# Revit family: QF_COMENDA_6G3232_6G3213_
name_source: partatom
category: Attrezzature speciali
units: mm (PartAtom-declared; Revit-internal decimal feet)

## family parameters
Basato su piano di lavoro = No
Condiviso = No
Numero OmniClass = 23.40.40.14
Punto di calcolo locali = No
Quota connettore circolare = Usa diametro
Sempre verticale = Sì
Taglio con vuoti quando caricato = No
Tipo di parte = Normale
Titolo OmniClass = Food Service Equipment

## types (2) — shared parameters
Altezza allacciamento elettrico da pavimento finito = 365 mm  [stored 1.19751 ft]
Altezza da terra raccordo acqua calda = 230 mm  [stored 0.754593 ft]
Altezza dello scarico diretto acqua da pavimento finito = 230 mm  [stored 0.754593 ft]
Corrente di funzionamento normale = 12 A
Diametro dello scarico diretto di acqua = 1 1/2"
Diametro raccordo acqua calda = 1"
Fase = 3
Frequenza = 50 Hz
Lunghezza = 740 mm  [stored 2.42782 ft]
Numero dei poli = 3
Peso netto = 150.00 kg
Potenza elettrica = 7500 W
Pressione minima acqua calda = 2000.0 Pa
Produttore = COMENDA
Profondità = 845 mm  [stored 2.77231 ft]
Protezione contro le sovracorrenti = 16 A
Temperatura raccomandata per acqua calda = 50 °C
URL = www.comenda.eu
URL catalogo = https://comenda.eu
zero-valued in all types: Prospetto di default

## per-type parameters (varying)
| type | Altezza | Descrizione | Modello | Tensione |
| 6G3232 | 1695 mm | THREE-PHASE FRONT LOADING POTWASHER  WITH RCD | G-EVO 50 R RCD | 400 V |
| 6G3213 | 1845 mm | THREE-PHASE FRONT LOADING POTWASHER WITH RCD | G-EVO 50H R RCD | 380 V |

note: [stored X ft] marks values corroborated as IEEE doubles in the binary element streams (Revit-internal decimal feet)

## geometry (parser evidence)
native form markers: Sweep x4
no freeform markers — native parametric forms only
